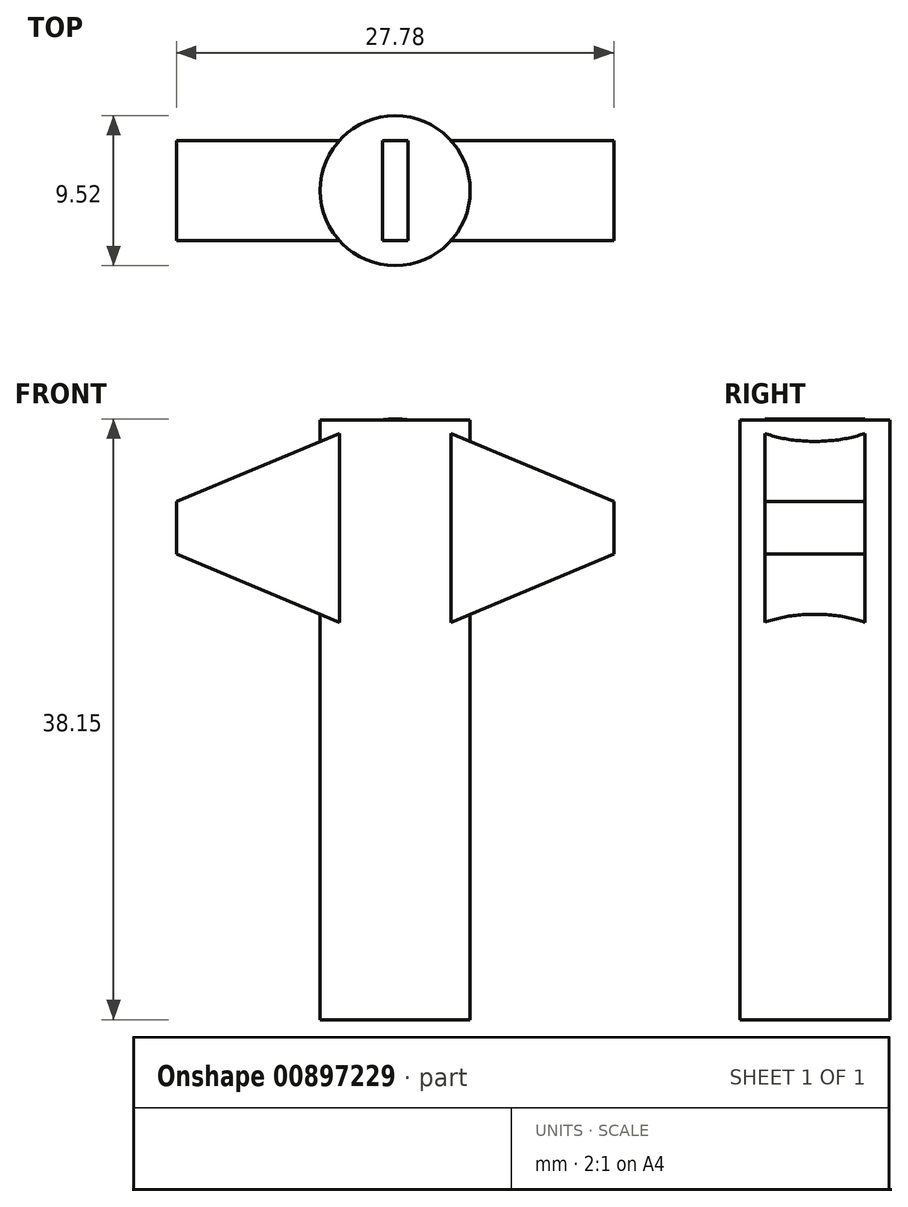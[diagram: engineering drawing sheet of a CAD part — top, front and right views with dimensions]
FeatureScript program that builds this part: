
annotation { "Feature Type Name" : "Feature", "Feature Type Description" : "" }
export const myFeature = defineFeature(function(context is Context, id is Id, definition is map)
    precondition{}
    {
        {
            var Q0;
            Q0=qCreatedBy(makeId("Top.planeOp"),FACE);
            var sketch = newSketch(context, id + "F0", { "sketchPlane" : qUnion([Q0])});
            skCircle(sketch, "E0", {"center": v(0, 0) * mm, "radius": 4.76 * mm});
            skSolve(sketch);
        }
        {
            var Q0;
            Q0 = qSketchRegion(id + "F0", true);
            extrude(context, id + "F1", {"entities" : qUnion([Q0]), "depth" : 38.1 * mm, "offsetDistance" : 25.4 * mm});
        }
        {
            var Q0;
            Q0=qCreatedBy(makeId("Front.planeOp"),FACE);
            var sketch = newSketch(context, id + "F2", { "sketchPlane" : qUnion([Q0])});
            skLineSegment(sketch, "E1.left", {"start": v(13.9, 29.58) * mm, "end": v(13.9, 32.9) * mm});
            skLineSegment(sketch, "E1.right", {"start": v(-13.9, 29.58) * mm, "end": v(-13.9, 32.9) * mm});
            skPoint(sketch, "E1.middle", {"position": v(0, 31.24) * mm});
            skArc(sketch, "E2", {"start": v(-2.67, 24.87) * mm, "mid": v(0, 24.34) * mm, "end": v(2.67, 24.87) * mm});
            skLineSegment(sketch, "E3", {"start": v(-13.9, 32.9) * mm, "end": v(-2.67, 37.61) * mm});
            skLineSegment(sketch, "E4", {"start": v(-13.9, 29.58) * mm, "end": v(-2.67, 24.87) * mm});
            skLineSegment(sketch, "E5", {"start": v(13.9, 29.58) * mm, "end": v(2.67, 24.87) * mm});
            skLineSegment(sketch, "E6", {"start": v(13.9, 32.9) * mm, "end": v(2.67, 37.61) * mm});
            skArc(sketch, "E7.trimOffspring", {"start": v(2.67, 37.61) * mm, "mid": v(0, 38.15) * mm, "end": v(-2.67, 37.61) * mm});
            skSolve(sketch);
        }
        {
            var Q0;
            Q0 = qSketchRegion(id + "F2", true);
            extrude(context, id + "F3", {"entities" : qUnion([Q0]), "operationType" : NewBodyOperationType.ADD, "endBound" : BoundingType.SYMMETRIC, "depth" : 6.35 * mm, "offsetDistance" : 25.4 * mm});
        }
    });
